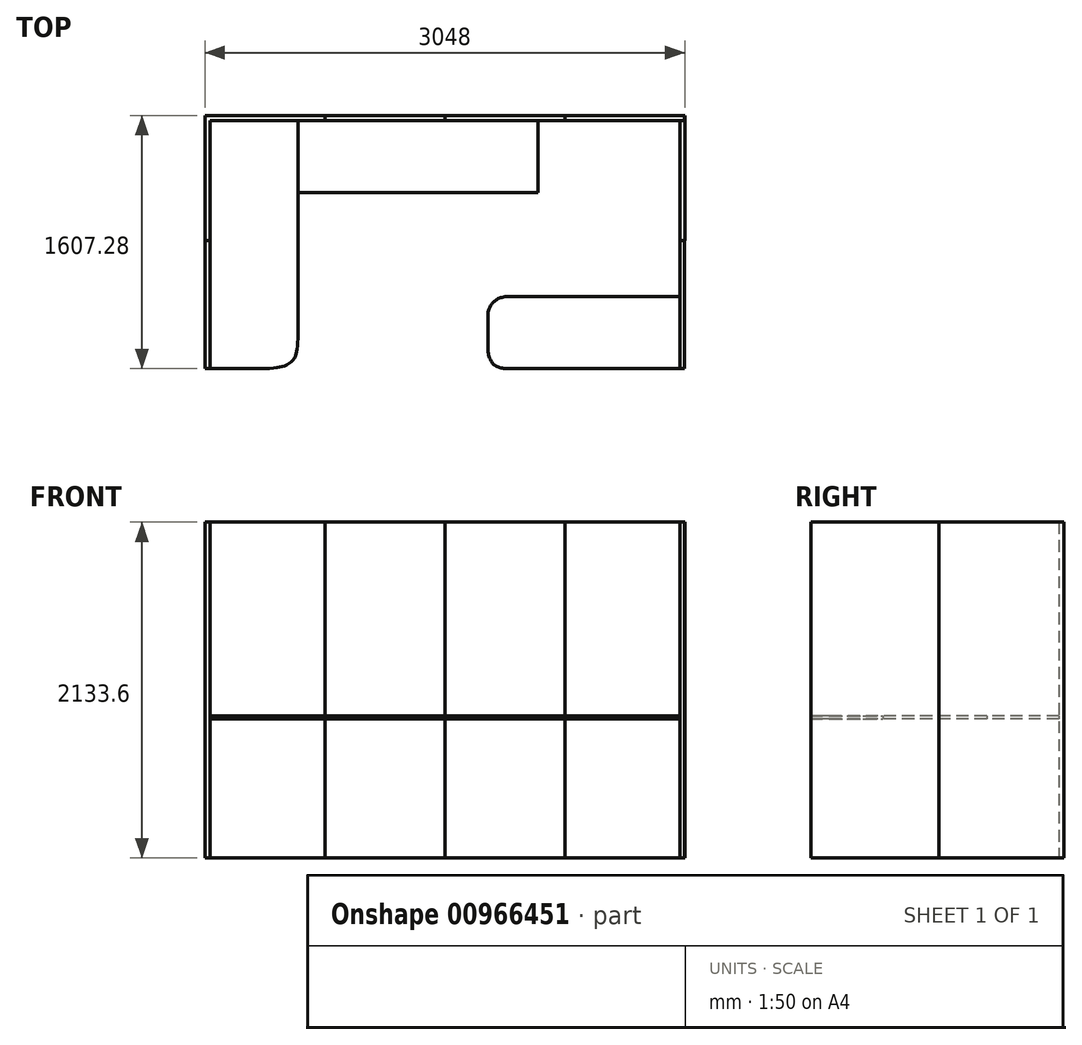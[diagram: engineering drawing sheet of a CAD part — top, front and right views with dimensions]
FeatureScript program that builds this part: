
annotation { "Feature Type Name" : "Feature", "Feature Type Description" : "" }
export const myFeature = defineFeature(function(context is Context, id is Id, definition is map)
    precondition{}
    {
        {
            var Q0;
            Q0=qCreatedBy(makeId("Top.planeOp"),FACE);
            var sketch = newSketch(context, id + "F0", { "sketchPlane" : qUnion([Q0])});
            skLineSegment(sketch, "E0.bottom", {"start": v(1524, -914.4) * mm, "end": v(-1524, -914.4) * mm});
            skLineSegment(sketch, "E0.top", {"start": v(1524, 914.4) * mm, "end": v(-1524, 914.4) * mm});
            skLineSegment(sketch, "E0.left", {"start": v(1524, -914.4) * mm, "end": v(1524, 914.4) * mm});
            skLineSegment(sketch, "E0.right", {"start": v(-1524, -914.4) * mm, "end": v(-1524, 914.4) * mm});
            skPoint(sketch, "E0.middle", {"position": v(0, 0) * mm});
            skSolve(sketch);
        }
        {
            var Q0;
            Q0=makeQuery(id+"F0.imprint","IMPRINT",FACE,{"disambiguationData":[TD([[makeQuery(id+"F0.imprint","IMPRINT",EDGE,{"derivedFrom":sQuery(id+"F0.wireOp",EDGE,"E0.bottom")}),-1.0]])]});
            var sketch = newSketch(context, id + "F1", { "sketchPlane" : qUnion([Q0])});
            skLineSegment(sketch, "E1.bottom", {"start": v(-1522.13, -706.61) * mm, "end": v(-1490.38, -706.61) * mm});
            skLineSegment(sketch, "E1.top", {"start": v(-1522.13, 106.19) * mm, "end": v(-1490.38, 106.19) * mm});
            skLineSegment(sketch, "E1.left", {"start": v(-1522.13, -706.61) * mm, "end": v(-1522.13, 106.19) * mm});
            skLineSegment(sketch, "E1.right", {"start": v(-1490.38, -706.61) * mm, "end": v(-1490.38, 106.19) * mm});
            skLineSegment(sketch, "E2.top", {"start": v(-1522.13, 868.19) * mm, "end": v(-1490.38, 868.19) * mm});
            skLineSegment(sketch, "E2.left", {"start": v(-1522.13, 106.19) * mm, "end": v(-1522.13, 868.19) * mm});
            skLineSegment(sketch, "E2.right", {"start": v(-1490.38, 106.19) * mm, "end": v(-1490.38, 868.19) * mm});
            skLineSegment(sketch, "E3.bottom", {"start": v(-1522.13, 868.19) * mm, "end": v(-760.13, 868.19) * mm});
            skLineSegment(sketch, "E3.top", {"start": v(-1522.13, 899.94) * mm, "end": v(-760.13, 899.94) * mm});
            skLineSegment(sketch, "E3.left", {"start": v(-1522.13, 868.19) * mm, "end": v(-1522.13, 899.94) * mm});
            skLineSegment(sketch, "E3.right", {"start": v(-760.13, 868.19) * mm, "end": v(-760.13, 899.94) * mm});
            skLineSegment(sketch, "E4.bottom", {"start": v(-760.13, 899.94) * mm, "end": v(1.87, 899.94) * mm});
            skLineSegment(sketch, "E4.top", {"start": v(-760.13, 868.19) * mm, "end": v(1.87, 868.19) * mm});
            skLineSegment(sketch, "E4.left", {"start": v(-760.13, 899.94) * mm, "end": v(-760.13, 868.19) * mm});
            skLineSegment(sketch, "E4.right", {"start": v(1.87, 899.94) * mm, "end": v(1.87, 868.19) * mm});
            skLineSegment(sketch, "E5.bottom", {"start": v(1.87, 899.94) * mm, "end": v(763.87, 899.94) * mm});
            skLineSegment(sketch, "E5.top", {"start": v(1.87, 868.19) * mm, "end": v(763.87, 868.19) * mm});
            skLineSegment(sketch, "E5.right", {"start": v(763.87, 899.94) * mm, "end": v(763.87, 868.19) * mm});
            skLineSegment(sketch, "E6.bottom", {"start": v(763.87, 899.94) * mm, "end": v(1525.87, 899.94) * mm});
            skLineSegment(sketch, "E6.top", {"start": v(763.87, 868.19) * mm, "end": v(1525.87, 868.19) * mm});
            skLineSegment(sketch, "E6.right", {"start": v(1525.87, 899.94) * mm, "end": v(1525.87, 868.19) * mm});
            skLineSegment(sketch, "E7.bottom", {"start": v(1525.87, 868.19) * mm, "end": v(1494.12, 868.19) * mm});
            skLineSegment(sketch, "E7.top", {"start": v(1525.87, 106.19) * mm, "end": v(1494.12, 106.19) * mm});
            skLineSegment(sketch, "E7.left", {"start": v(1525.87, 868.19) * mm, "end": v(1525.87, 106.19) * mm});
            skLineSegment(sketch, "E7.right", {"start": v(1494.12, 868.19) * mm, "end": v(1494.12, 106.19) * mm});
            skLineSegment(sketch, "E8.bottom", {"start": v(1494.12, 106.19) * mm, "end": v(1525.87, 106.19) * mm});
            skLineSegment(sketch, "E8.top", {"start": v(1494.12, -706.61) * mm, "end": v(1525.87, -706.61) * mm});
            skLineSegment(sketch, "E8.left", {"start": v(1494.12, 106.19) * mm, "end": v(1494.12, -706.61) * mm});
            skLineSegment(sketch, "E8.right", {"start": v(1525.87, 106.19) * mm, "end": v(1525.87, -706.61) * mm});
            skSolve(sketch);
        }
        {
            var Q0;
            Q0=makeQuery(id+"F1.imprint","IMPRINT",FACE,{"disambiguationData":[TD([[makeQuery(id+"F1.imprint","IMPRINT",EDGE,{"derivedFrom":sQuery(id+"F1.wireOp",EDGE,"E1.bottom")}),1.0]])]});
            extrude(context, id + "F2", {"entities" : qUnion([Q0]), "depth" : 2133.6 * mm, "offsetDistance" : 25.4 * mm});
        }
        {
            var Q0;
            Q0=makeQuery(id+"F1.imprint","IMPRINT",FACE,{"disambiguationData":[TD([[makeQuery(id+"F1.imprint","IMPRINT",EDGE,{"derivedFrom":sQuery(id+"F1.wireOp",EDGE,"E1.top")}),1.0]])]});
            extrude(context, id + "F3", {"entities" : qUnion([Q0]), "depth" : 2133.6 * mm, "offsetDistance" : 25.4 * mm});
        }
        {
            var Q0;
            Q0=makeQuery(id+"F1.imprint","IMPRINT",FACE,{"disambiguationData":[TD([[makeQuery(id+"F1.imprint","IMPRINT",EDGE,{"derivedFrom":sQuery(id+"F1.wireOp",EDGE,"E2.top")}),1.0]])]});
            extrude(context, id + "F4", {"entities" : qUnion([Q0]), "operationType" : NewBodyOperationType.ADD, "depth" : 2133.6 * mm, "offsetDistance" : 25.4 * mm});
        }
        {
            var Q0;
            Q0=makeQuery(id+"F1.imprint","IMPRINT",FACE,{"disambiguationData":[TD([[makeQuery(id+"F1.imprint","IMPRINT",EDGE,{"derivedFrom":sQuery(id+"F1.wireOp",EDGE,"E3.right")}),-1.0]])]});
            extrude(context, id + "F5", {"entities" : qUnion([Q0]), "depth" : 2133.6 * mm, "offsetDistance" : 25.4 * mm});
        }
        {
            var Q0;
            Q0=makeQuery(id+"F1.imprint","IMPRINT",FACE,{"disambiguationData":[TD([[makeQuery(id+"F1.imprint","IMPRINT",EDGE,{"derivedFrom":sQuery(id+"F1.wireOp",EDGE,"E4.right")}),1.0]])]});
            extrude(context, id + "F6", {"entities" : qUnion([Q0]), "depth" : 2133.6 * mm, "offsetDistance" : 25.4 * mm});
        }
        {
            var Q0;
            {var subQ4=sQuery(id+"F1.wireOp",EDGE,"E5.right");Q0=makeQuery(id+"F1.imprint","IMPRINT",FACE,{"disambiguationData":[TD([[makeQuery(id+"F1.imprint","IMPRINT",EDGE,{"derivedFrom":subQ4}),1.0]])]});}
            extrude(context, id + "F7", {"entities" : qUnion([Q0]), "depth" : 2133.6 * mm, "offsetDistance" : 25.4 * mm});
        }
        {
            var Q0;
            {var subQ0=sQuery(id+"F1.wireOp",EDGE,"E7.left");Q0=makeQuery(id+"F1.imprint","IMPRINT",FACE,{"disambiguationData":[TD([[makeQuery(id+"F1.imprint","IMPRINT",EDGE,{"derivedFrom":subQ0}),-1.0]])]});}
            var Q1;
            {var subQ0=sQuery(id+"F1.wireOp",EDGE,"E7.right");Q1=makeQuery(id+"F1.imprint","IMPRINT",FACE,{"disambiguationData":[TD([[makeQuery(id+"F1.imprint","IMPRINT",EDGE,{"derivedFrom":subQ0}),1.0]])]});}
            var Q2;
            {var subQ0=sQuery(id+"F1.wireOp",EDGE,"E6.right");Q2=makeQuery(id+"F1.imprint","IMPRINT",FACE,{"disambiguationData":[TD([[makeQuery(id+"F1.imprint","IMPRINT",EDGE,{"derivedFrom":subQ0}),-1.0]])]});}
            extrude(context, id + "F8", {"entities" : qUnion([Q0, Q1, Q2]), "depth" : 2133.6 * mm, "offsetDistance" : 25.4 * mm});
        }
        {
            var Q0;
            {var subQ0=sQuery(id+"F1.wireOp",EDGE,"E8.left");Q0=makeQuery(id+"F1.imprint","IMPRINT",FACE,{"disambiguationData":[TD([[makeQuery(id+"F1.imprint","IMPRINT",EDGE,{"derivedFrom":subQ0}),1.0]])]});}
            extrude(context, id + "F9", {"entities" : qUnion([Q0]), "depth" : 2133.6 * mm, "offsetDistance" : 25.4 * mm});
        }
        {
            var Q0;
            Q0=makeQuery(id+"F0.imprint","IMPRINT",FACE,{"disambiguationData":[TD([[makeQuery(id+"F0.imprint","IMPRINT",EDGE,{"derivedFrom":sQuery(id+"F0.wireOp",EDGE,"E0.bottom")}),-1.0]])]});
            cPlane(context, id + "F10", {"entities" : qUnion([Q0]), "cplaneType" : CPlaneType.OFFSET, "offset" : 882.65 * mm, "width" : 152.4 * mm, "height" : 152.4 * mm});
        }
        {
            var Q0;
            Q0=qCreatedBy(id+"F10.planeOp",FACE);
            var sketch = newSketch(context, id + "F11", { "sketchPlane" : qUnion([Q0])});
            skLineSegment(sketch, "E9.bottom", {"start": v(-1489.99, 867.46) * mm, "end": v(-931.19, 867.46) * mm});
            skLineSegment(sketch, "E9.top", {"start": v(-1489.99, -707.34) * mm, "end": v(-1165.97, -707.34) * mm});
            skLineSegment(sketch, "E9.left", {"start": v(-1489.99, 867.46) * mm, "end": v(-1489.99, -707.34) * mm});
            skLineSegment(sketch, "E9.right", {"start": v(-931.19, 867.46) * mm, "end": v(-931.19, -489.12) * mm});
            skLineSegment(sketch, "E10.bottom", {"start": v(1494, -707.26) * mm, "end": v(401.8, -707.26) * mm});
            skLineSegment(sketch, "E10.top", {"start": v(1494, -250.06) * mm, "end": v(401.8, -250.06) * mm});
            skLineSegment(sketch, "E10.left", {"start": v(1494, -707.26) * mm, "end": v(1494, -250.06) * mm});
            skLineSegment(sketch, "E10.right", {"start": v(274.8, -580.26) * mm, "end": v(274.8, -377.06) * mm});
            skLineSegment(sketch, "E11.bottom", {"start": v(-931.19, 867.46) * mm, "end": v(592.81, 867.46) * mm});
            skLineSegment(sketch, "E11.top", {"start": v(-931.19, 410.26) * mm, "end": v(592.81, 410.26) * mm});
            skLineSegment(sketch, "E11.left", {"start": v(-931.19, 867.46) * mm, "end": v(-931.19, 410.26) * mm});
            skLineSegment(sketch, "E11.right", {"start": v(592.81, 867.46) * mm, "end": v(592.81, 410.26) * mm});
            skPoint(sketch, "E12", {"position": v(-1165.97, -707.34) * mm});
            skPoint(sketch, "E13", {"position": v(-931.19, -489.12) * mm});
            skFitSpline(sketch, "E14", {"points": [v(-1165.97, -707.34) * mm, v(-968.9, -660.78) * mm, v(-931.19, -489.12) * mm], "startDerivative": vector(722, 0) * mm, "endDerivative": vector(0, 699.8) * mm});
            skFitSpline(sketch, "E15", {"points": [v(274.8, -377.06) * mm, v(311.29, -285.21) * mm, v(401.8, -250.06) * mm], "startDerivative": vector(0, 239.14) * mm, "endDerivative": vector(223.09, 0) * mm});
            skFitSpline(sketch, "E16", {"points": [v(274.8, -580.26) * mm, v(310.26, -678.8) * mm, v(401.8, -707.26) * mm], "startDerivative": vector(0, -155.23) * mm, "endDerivative": vector(195.28, 0) * mm});
            skPoint(sketch, "E17.orphan", {"position": v(274.8, -707.26) * mm});
            skPoint(sketch, "E18.orphan", {"position": v(274.8, -250.06) * mm});
            skSolve(sketch);
        }
        {
            var Q0;
            {var subQ3=sQuery(id+"F11.wireOp",EDGE,"E9.bottom");Q0=makeQuery(id+"F11.imprint","IMPRINT",FACE,{"disambiguationData":[TD([[makeQuery(id+"F11.imprint","IMPRINT",EDGE,{"derivedFrom":subQ3}),-1.0]])]});}
            extrude(context, id + "F12", {"entities" : qUnion([Q0]), "depth" : 19.05 * mm, "offsetDistance" : 25.4 * mm});
        }
        {
            var Q0;
            Q0=makeQuery(id+"F11.imprint","IMPRINT",FACE,{"disambiguationData":[TD([[makeQuery(id+"F11.imprint","IMPRINT",EDGE,{"derivedFrom":sQuery(id+"F11.wireOp",EDGE,"E10.bottom")}),-1.0]])]});
            extrude(context, id + "F13", {"entities" : qUnion([Q0]), "operationType" : NewBodyOperationType.ADD, "depth" : 19.05 * mm, "offsetDistance" : 25.4 * mm});
        }
        {
            var Q0;
            {var subQ0=sQuery(id+"F11.wireOp",EDGE,"E11.bottom");var subQ2=sQuery(id+"F11.wireOp",EDGE,"E9.bottom");Q0=qUnion([makeQuery(id+"F11.imprint","IMPRINT",FACE,{"disambiguationData":[TD([[makeQuery(id+"F11.imprint","IMPRINT",EDGE,{"derivedFrom":sQuery(id+"F11.wireOp",EDGE,"E10.bottom")}),-1.0]])]}),makeQuery(id+"F11.imprint","IMPRINT",FACE,{"disambiguationData":[TD([[makeQuery(id+"F11.imprint","IMPRINT",EDGE,{"derivedFrom":subQ2}),-1.0]])]}),makeQuery(id+"F11.imprint","IMPRINT",FACE,{"disambiguationData":[TD([[makeQuery(id+"F11.imprint","IMPRINT",EDGE,{"derivedFrom":subQ0}),-1.0]])]})]);}
            extrude(context, id + "F14", {"entities" : qUnion([Q0]), "depth" : 19.05 * mm, "offsetDistance" : 25.4 * mm});
        }
    });
